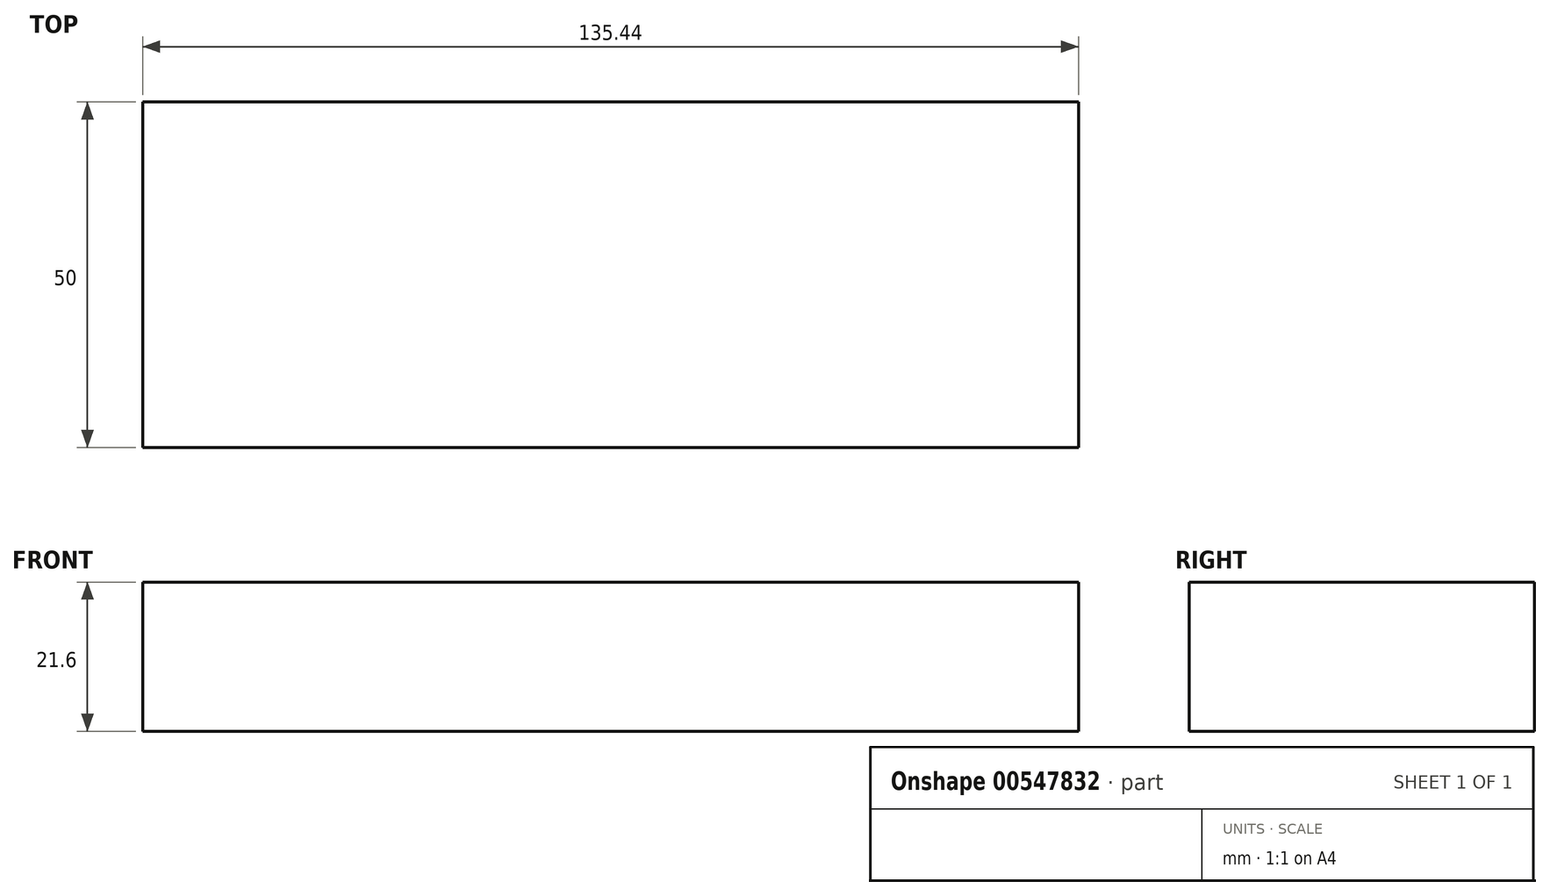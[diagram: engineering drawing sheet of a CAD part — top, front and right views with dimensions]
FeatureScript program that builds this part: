
annotation { "Feature Type Name" : "Feature", "Feature Type Description" : "" }
export const myFeature = defineFeature(function(context is Context, id is Id, definition is map)
    precondition{}
    {
        {
            var Q0;
            Q0=qCreatedBy(makeId("Front.planeOp"),FACE);
            var sketch = newSketch(context, id + "F0", { "sketchPlane" : qUnion([Q0])});
            skLineSegment(sketch, "E0.bottom", {"start": v(-64.99, 21.6) * mm, "end": v(70.45, 21.6) * mm});
            skLineSegment(sketch, "E0.top", {"start": v(-64.99, 0) * mm, "end": v(70.45, 0) * mm});
            skLineSegment(sketch, "E0.left", {"start": v(-64.99, 21.6) * mm, "end": v(-64.99, 0) * mm});
            skLineSegment(sketch, "E0.right", {"start": v(70.45, 21.6) * mm, "end": v(70.45, 0) * mm});
            skSolve(sketch);
        }
        {
            var Q0;
            Q0 = qSketchRegion(id + "F0", true);
            extrude(context, id + "F1", {"entities" : qUnion([Q0]), "depth" : 50 * mm, "offsetDistance" : 25 * mm});
        }
    });
